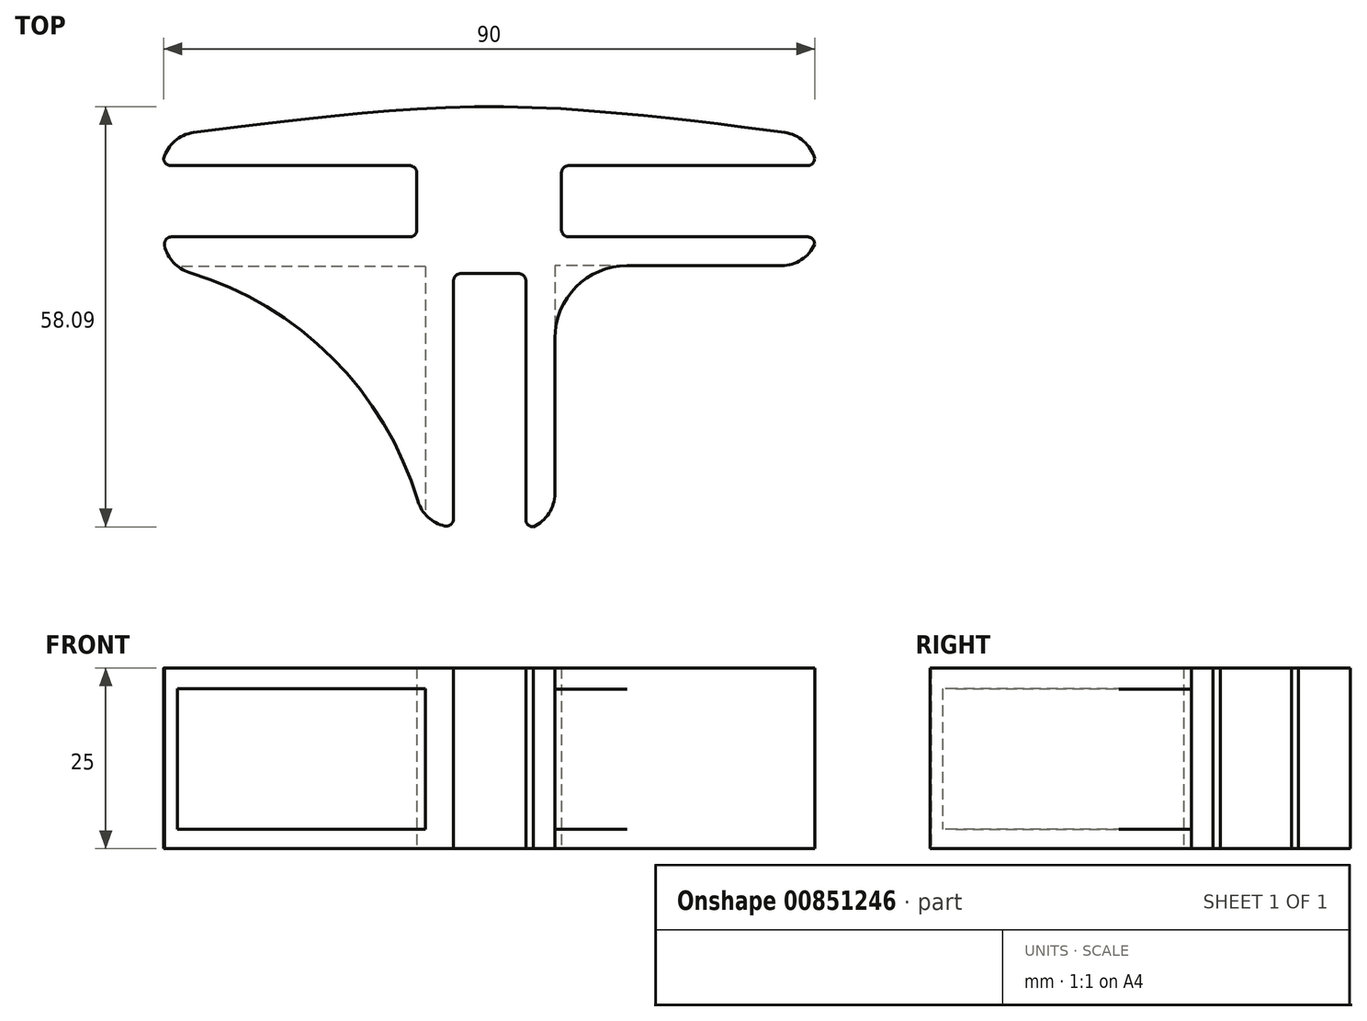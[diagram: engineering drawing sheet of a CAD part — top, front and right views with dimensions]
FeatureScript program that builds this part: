
annotation { "Feature Type Name" : "Feature", "Feature Type Description" : "" }
export const myFeature = defineFeature(function(context is Context, id is Id, definition is map)
    precondition{}
    {
        {
            var Q0;
            Q0=qCreatedBy(makeId("Top.planeOp"),FACE);
            var sketch = newSketch(context, id + "F0", { "sketchPlane" : qUnion([Q0])});
            skLineSegment(sketch, "E0.bottom", {"start": v(45, 45) * mm, "end": v(-45, 45) * mm, "construction": true});
            skLineSegment(sketch, "E0.top", {"start": v(45, -45) * mm, "end": v(-45, -45) * mm, "construction": true});
            skLineSegment(sketch, "E0.left", {"start": v(45, 45) * mm, "end": v(45, -45) * mm, "construction": true});
            skLineSegment(sketch, "E0.right", {"start": v(-45, 45) * mm, "end": v(-45, -45) * mm, "construction": true});
            skLineSegment(sketch, "E1", {"start": v(0, 45) * mm, "end": v(0, -45) * mm, "construction": true});
            skLineSegment(sketch, "E2", {"start": v(-45, 0) * mm, "end": v(45, 0) * mm, "construction": true});
            skLineSegment(sketch, "E3", {"start": v(-45, 4.92) * mm, "end": v(45, 4.92) * mm, "construction": true});
            skLineSegment(sketch, "E4", {"start": v(-45, -4.92) * mm, "end": v(45, -4.92) * mm, "construction": true});
            skLineSegment(sketch, "E5", {"start": v(-45, 4.92) * mm, "end": v(-45, 8.92) * mm});
            skLineSegment(sketch, "E6", {"start": v(45, 4.92) * mm, "end": v(45, 8.92) * mm});
            skLineSegment(sketch, "E7", {"start": v(45, -4.92) * mm, "end": v(45, -8.92) * mm});
            skLineSegment(sketch, "E8", {"start": v(-45, -4.92) * mm, "end": v(-45, -5.06) * mm});
            skLineSegment(sketch, "E9", {"start": v(-4.92, -45) * mm, "end": v(-4.92, -10) * mm});
            skLineSegment(sketch, "E10", {"start": v(-4.92, -10) * mm, "end": v(5.08, -10) * mm});
            skLineSegment(sketch, "E11", {"start": v(5.08, -10) * mm, "end": v(5.08, -45) * mm});
            skLineSegment(sketch, "E12", {"start": v(45, -4.92) * mm, "end": v(10, -4.92) * mm});
            skLineSegment(sketch, "E13", {"start": v(10, -4.92) * mm, "end": v(10, 4.92) * mm});
            skLineSegment(sketch, "E14", {"start": v(10, 4.92) * mm, "end": v(45, 4.92) * mm});
            skLineSegment(sketch, "E15", {"start": v(-45, 4.92) * mm, "end": v(-10, 4.92) * mm});
            skLineSegment(sketch, "E16", {"start": v(-10, 4.92) * mm, "end": v(-10, -4.92) * mm});
            skLineSegment(sketch, "E17", {"start": v(-10, -4.92) * mm, "end": v(-45, -4.92) * mm});
            skLineSegment(sketch, "E18", {"start": v(-4.92, -45) * mm, "end": v(-5.06, -45) * mm});
            skLineSegment(sketch, "E19", {"start": v(5.08, -45) * mm, "end": v(9.08, -45) * mm});
            skArc(sketch, "E20", {"start": v(-9.85, -41.44) * mm, "mid": v(-21.68, -21.68) * mm, "end": v(-41.45, -9.84) * mm});
            skFitSpline(sketch, "E21", {"points": [v(-45, 8.92) * mm, v(-26.76, 11.24) * mm, v(0, 13.1) * mm, v(27.01, 11.24) * mm, v(45, 8.92) * mm], "startDerivative": vector(76.6, 11.1) * mm, "endDerivative": vector(75.75, -11.18) * mm});
            skPoint(sketch, "E22.visualSharp", {"position": v(-45, -8.92) * mm});
            skArc(sketch, "E22.filletArc", {"start": v(-45, -5.06) * mm, "mid": v(-44.01, -8.04) * mm, "end": v(-41.45, -9.84) * mm});
            skPoint(sketch, "E23.visualSharp", {"position": v(-8.92, -45) * mm});
            skArc(sketch, "E23.filletArc", {"start": v(-9.85, -41.44) * mm, "mid": v(-8.04, -44.01) * mm, "end": v(-5.06, -45) * mm});
            skLineSegment(sketch, "E24", {"start": v(45, -8.92) * mm, "end": v(9.08, -8.92) * mm});
            skLineSegment(sketch, "E25", {"start": v(9.08, -8.92) * mm, "end": v(9.08, -45) * mm});
            skSolve(sketch);
        }
        {
            var Q0;
            Q0=qSketchRegion(id+"F0",true);
            extrude(context, id + "F1", {"entities" : qUnion([Q0]), "depth" : 25 * mm, "offsetDistance" : 25 * mm});
        }
        {
            var Q0;
            Q0=makeQuery(id+"F1.opExtrude","SWEPT_EDGE",EDGE,{"disambiguationData":[OSD([sQuery(id+"F0.wireOp",EDGE,"E8"),sQuery(id+"F0.wireOp",EDGE,"E17")])]});
            var Q1;
            Q1=makeQuery(id+"F1.opExtrude","SWEPT_EDGE",EDGE,{"disambiguationData":[OSD([sQuery(id+"F0.wireOp",EDGE,"E5"),sQuery(id+"F0.wireOp",EDGE,"E15")])]});
            var Q2;
            Q2=makeQuery(id+"F1.opExtrude","SWEPT_EDGE",EDGE,{"disambiguationData":[OSD([sQuery(id+"F0.wireOp",EDGE,"WPb36Jyi-Yplt-UmGR-S4ml-xzFoEZJ1AGUH"),sQuery(id+"F0.wireOp",EDGE,"E9")])]});
            var Q3;
            Q3=makeQuery(id+"F1.opExtrude","SWEPT_EDGE",EDGE,{"disambiguationData":[OSD([sQuery(id+"F0.wireOp",EDGE,"mrf3EofF-n60g-gq5k-HxXF-4o4gbP8yl62G"),sQuery(id+"F0.wireOp",EDGE,"E11")])]});
            var Q4;
            Q4=makeQuery(id+"F1.opExtrude","SWEPT_EDGE",EDGE,{"disambiguationData":[OSD([sQuery(id+"F0.wireOp",EDGE,"E7"),sQuery(id+"F0.wireOp",EDGE,"E12")])]});
            var Q5;
            Q5=makeQuery(id+"F1.opExtrude","SWEPT_EDGE",EDGE,{"disambiguationData":[OSD([sQuery(id+"F0.wireOp",EDGE,"E6"),sQuery(id+"F0.wireOp",EDGE,"E14")])]});
            var Q6;
            Q6=makeQuery(id+"F1.opExtrude","SWEPT_EDGE",EDGE,{"disambiguationData":[OSD([sQuery(id+"F0.wireOp",EDGE,"MM1ln0Jl-5PRi-5D8f-pG0F-OAi5QMAfzF3z"),sQuery(id+"F0.wireOp",EDGE,"DjTs0NOw-kcec-RKhR-Ig24-jyuwGINhqP7C")])]});
            var Q7;
            Q7=makeQuery(id+"F1.opExtrude","SWEPT_EDGE",EDGE,{"disambiguationData":[OSD([sQuery(id+"F0.wireOp",EDGE,"lCwj412f-a0UU-974L-psAJ-6MNTU11T9Nfu"),sQuery(id+"F0.wireOp",EDGE,"LV4aiMub-avi9-516q-T3Iv-ZsKpD34xg9iY")])]});
            var Q8;
            Q8=makeQuery(id+"F1.opExtrude","SWEPT_EDGE",EDGE,{"disambiguationData":[OSD([sQuery(id+"F0.wireOp",EDGE,"E12"),sQuery(id+"F0.wireOp",EDGE,"E13")])]});
            var Q9;
            Q9=makeQuery(id+"F1.opExtrude","SWEPT_EDGE",EDGE,{"disambiguationData":[OSD([sQuery(id+"F0.wireOp",EDGE,"E13"),sQuery(id+"F0.wireOp",EDGE,"E14")])]});
            var Q10;
            Q10=makeQuery(id+"F1.opExtrude","SWEPT_EDGE",EDGE,{"disambiguationData":[OSD([sQuery(id+"F0.wireOp",EDGE,"E16"),sQuery(id+"F0.wireOp",EDGE,"E17")])]});
            var Q11;
            Q11=makeQuery(id+"F1.opExtrude","SWEPT_EDGE",EDGE,{"disambiguationData":[OSD([sQuery(id+"F0.wireOp",EDGE,"E15"),sQuery(id+"F0.wireOp",EDGE,"E16")])]});
            var Q12;
            Q12=makeQuery(id+"F1.opExtrude","SWEPT_EDGE",EDGE,{"disambiguationData":[OSD([sQuery(id+"F0.wireOp",EDGE,"4Qy6dOt6-SkNY-HZek-wTVB-erV8T1B4pnAX"),sQuery(id+"F0.wireOp",EDGE,"DjTs0NOw-kcec-RKhR-Ig24-jyuwGINhqP7C")])]});
            var Q13;
            Q13=makeQuery(id+"F1.opExtrude","SWEPT_EDGE",EDGE,{"disambiguationData":[OSD([sQuery(id+"F0.wireOp",EDGE,"LV4aiMub-avi9-516q-T3Iv-ZsKpD34xg9iY"),sQuery(id+"F0.wireOp",EDGE,"4Qy6dOt6-SkNY-HZek-wTVB-erV8T1B4pnAX")])]});
            fillet(context, id + "F2", {"entities" : qUnion([Q0, Q1, Q2, Q3, Q4, Q5, Q6, Q7, Q8, Q9, Q10, Q11, Q12, Q13]), "radius" : 1 * mm, "tangentPropagation" : true, "allowEdgeOverflow" : false});
        }
        {
            var Q0;
            Q0=makeQuery(id+"F1.opExtrude","SWEPT_FACE",FACE,{"disambiguationData":[OSD([sQuery(id+"F0.wireOp",EDGE,"E19")])]});
            var sketch = newSketch(context, id + "F3", { "sketchPlane" : qUnion([Q0])});
            skLineSegment(sketch, "E26.bottom", {"start": v(-8.81, 22.1) * mm, "end": v(-46.99, 22.1) * mm});
            skLineSegment(sketch, "E26.top", {"start": v(-8.81, 2.7) * mm, "end": v(-46.99, 2.7) * mm});
            skLineSegment(sketch, "E26.left", {"start": v(-8.81, 22.1) * mm, "end": v(-8.81, 2.7) * mm});
            skLineSegment(sketch, "E26.right", {"start": v(-46.99, 22.1) * mm, "end": v(-46.99, 2.7) * mm});
            skLineSegment(sketch, "E27.right", {"start": v(52.1, 22.23) * mm, "end": v(52.1, 2.46) * mm});
            skLineSegment(sketch, "E28", {"start": v(52.1, 22.23) * mm, "end": v(8.93, 22.23) * mm});
            skLineSegment(sketch, "E29", {"start": v(8.93, 22.23) * mm, "end": v(8.93, 2.46) * mm});
            skLineSegment(sketch, "E30", {"start": v(8.93, 2.46) * mm, "end": v(52.1, 2.46) * mm});
            skSolve(sketch);
        }
        {
            var Q0;
            Q0=makeQuery(id+"F3.imprint","IMPRINT",FACE,{"disambiguationData":[TD([[makeQuery(id+"F3.imprint","IMPRINT",EDGE,{"derivedFrom":sQuery(id+"F3.wireOp",EDGE,"E26.bottom")}),1.0]])]});
            var Q1;
            Q1=makeQuery(id+"F3.imprint","IMPRINT",FACE,{"disambiguationData":[TD([[makeQuery(id+"F3.imprint","IMPRINT",EDGE,{"derivedFrom":sQuery(id+"F3.wireOp",EDGE,"E27.bottom")}),-1.0]])]});
            extrude(context, id + "F4", {"entities" : qUnion([Q0, Q1]), "operationType" : NewBodyOperationType.REMOVE, "oppositeDirection" : true, "depth" : 36 * mm, "offsetDistance" : 25 * mm});
        }
        {
            var Q0;
            Q0=makeQuery(id+"F1.opExtrude","SWEPT_EDGE",EDGE,{"disambiguationData":[OSD([sQuery(id+"F0.wireOp",EDGE,"E5"),sQuery(id+"F0.wireOp",EDGE,"E21")])]});
            var Q1;
            Q1=makeQuery(id+"F1.opExtrude","SWEPT_EDGE",EDGE,{"disambiguationData":[OSD([sQuery(id+"F0.wireOp",EDGE,"E6"),sQuery(id+"F0.wireOp",EDGE,"E21")])]});
            fillet(context, id + "F5", {"entities" : qUnion([Q0, Q1]), "radius" : 5 * mm, "tangentPropagation" : true, "allowEdgeOverflow" : false});
        }
        {
            var Q0;
            Q0=makeQuery(id+"F3.imprint","IMPRINT",FACE,{"disambiguationData":[TD([[makeQuery(id+"F3.imprint","IMPRINT",EDGE,{"derivedFrom":sQuery(id+"F3.wireOp",EDGE,"E27.right")}),-1.0]])]});
            extrude(context, id + "F6", {"entities" : qUnion([Q0]), "operationType" : NewBodyOperationType.REMOVE, "oppositeDirection" : true, "depth" : 36 * mm, "offsetDistance" : 25 * mm});
        }
        {
            var Q0;
            Q0=makeQuery(id+"F1.opExtrude","SWEPT_EDGE",EDGE,{"disambiguationData":[OSD([sQuery(id+"F0.wireOp",EDGE,"E24"),sQuery(id+"F0.wireOp",EDGE,"E25")])]});
            fillet(context, id + "F7", {"entities" : qUnion([Q0]), "radius" : 10 * mm, "tangentPropagation" : true, "allowEdgeOverflow" : false});
        }
        {
            var Q0;
            Q0=makeQuery(id+"F1.opExtrude","SWEPT_FACE",FACE,{"disambiguationData":[OSD([sQuery(id+"F0.wireOp",EDGE,"E19")])]});
            var sketch = newSketch(context, id + "F8", { "sketchPlane" : qUnion([Q0])});
            skLineSegment(sketch, "E31.bottom", {"start": v(9.08, 22.06) * mm, "end": v(43.03, 22.06) * mm});
            skLineSegment(sketch, "E31.top", {"start": v(9.08, 2.72) * mm, "end": v(43.03, 2.72) * mm});
            skLineSegment(sketch, "E31.left", {"start": v(9.08, 22.06) * mm, "end": v(9.08, 2.72) * mm});
            skLineSegment(sketch, "E31.right", {"start": v(43.03, 22.06) * mm, "end": v(43.03, 2.72) * mm});
            skSolve(sketch);
        }
        {
            var Q0;
            Q0 = qSketchRegion(id + "F8", true);
            extrude(context, id + "F9", {"entities" : qUnion([Q0]), "operationType" : NewBodyOperationType.REMOVE, "oppositeDirection" : true, "depth" : 36.1 * mm, "offsetDistance" : 25 * mm});
        }
        {
            var Q0;
            Q0=makeQuery(id+"F1.opExtrude","SWEPT_EDGE",EDGE,{"disambiguationData":[OSD([sQuery(id+"F0.wireOp",EDGE,"E19"),sQuery(id+"F0.wireOp",EDGE,"E25")])]});
            var Q1;
            Q1=makeQuery(id+"F1.opExtrude","SWEPT_EDGE",EDGE,{"disambiguationData":[OSD([sQuery(id+"F0.wireOp",EDGE,"E7"),sQuery(id+"F0.wireOp",EDGE,"E24")])]});
            fillet(context, id + "F10", {"entities" : qUnion([Q0, Q1]), "radius" : 5 * mm, "tangentPropagation" : true, "allowEdgeOverflow" : false});
        }
    });
